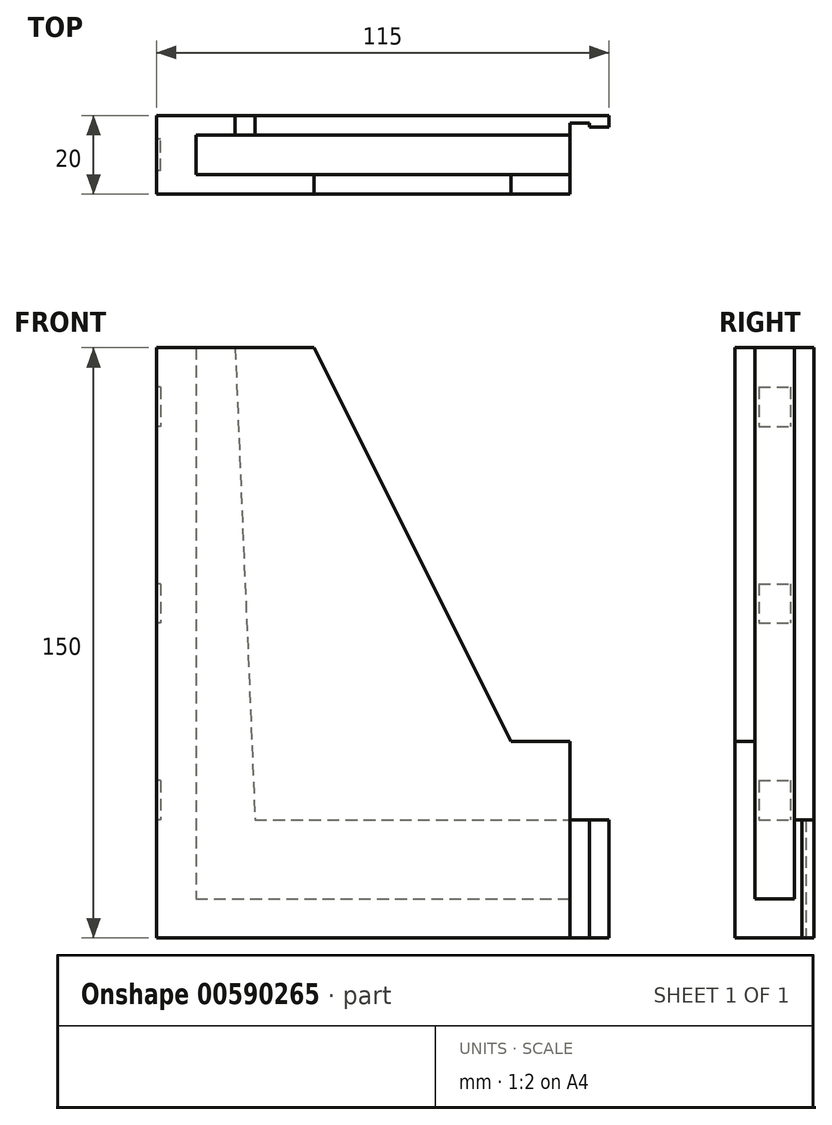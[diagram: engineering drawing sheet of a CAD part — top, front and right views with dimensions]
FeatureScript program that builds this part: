
annotation { "Feature Type Name" : "Feature", "Feature Type Description" : "" }
export const myFeature = defineFeature(function(context is Context, id is Id, definition is map)
    precondition{}
    {
        {
            var Q0;
            Q0=qCreatedBy(makeId("Top.planeOp"),FACE);
            var sketch = newSketch(context, id + "F0", { "sketchPlane" : qUnion([Q0])});
            skLineSegment(sketch, "E0.bottom", {"start": v(0, 0) * mm, "end": v(95, 0) * mm});
            skLineSegment(sketch, "E0.top", {"start": v(0, 5) * mm, "end": v(95, 5) * mm});
            skLineSegment(sketch, "E0.left", {"start": v(0, 0) * mm, "end": v(0, 5) * mm});
            skLineSegment(sketch, "E0.right", {"start": v(95, 0) * mm, "end": v(95, 5) * mm});
            skSolve(sketch);
        }
        {
            var Q0;
            Q0=makeQuery(id+"F0.imprint","IMPRINT",FACE,{"disambiguationData":[TD([[makeQuery(id+"F0.imprint","IMPRINT",EDGE,{"derivedFrom":sQuery(id+"F0.wireOp",EDGE,"E0.bottom")}),1.0]])]});
            extrude(context, id + "F1", {"entities" : qUnion([Q0]), "depth" : 50 * mm, "offsetDistance" : 25 * mm});
        }
        {
            var Q0;
            Q0=qCreatedBy(makeId("Top.planeOp"),FACE);
            var sketch = newSketch(context, id + "F2", { "sketchPlane" : qUnion([Q0])});
            skLineSegment(sketch, "E1.bottom", {"start": v(0, 5) * mm, "end": v(95, 5) * mm});
            skLineSegment(sketch, "E1.top", {"start": v(0, 15) * mm, "end": v(95, 15) * mm});
            skLineSegment(sketch, "E1.left", {"start": v(0, 5) * mm, "end": v(0, 15) * mm});
            skLineSegment(sketch, "E1.right", {"start": v(95, 5) * mm, "end": v(95, 15) * mm});
            skSolve(sketch);
        }
        {
            var Q0;
            Q0 = qSketchRegion(id + "F2", true);
            extrude(context, id + "F3", {"entities" : qUnion([Q0]), "operationType" : NewBodyOperationType.ADD, "depth" : 10 * mm, "offsetDistance" : 25 * mm});
        }
        {
            var Q0;
            Q0=qCreatedBy(makeId("Top.planeOp"),FACE);
            var sketch = newSketch(context, id + "F4", { "sketchPlane" : qUnion([Q0])});
            skLineSegment(sketch, "E2.bottom", {"start": v(0, 15) * mm, "end": v(95, 15) * mm});
            skLineSegment(sketch, "E2.top", {"start": v(0, 20) * mm, "end": v(95, 20) * mm});
            skLineSegment(sketch, "E2.left", {"start": v(0, 15) * mm, "end": v(0, 20) * mm});
            skLineSegment(sketch, "E2.right", {"start": v(95, 15) * mm, "end": v(95, 20) * mm});
            skLineSegment(sketch, "E3.bottom", {"start": v(95, 20) * mm, "end": v(100, 20) * mm});
            skLineSegment(sketch, "E3.top", {"start": v(95, 18) * mm, "end": v(100, 18) * mm});
            skLineSegment(sketch, "E3.left", {"start": v(95, 20) * mm, "end": v(95, 18) * mm});
            skLineSegment(sketch, "E3.right", {"start": v(100, 20) * mm, "end": v(100, 18) * mm});
            skLineSegment(sketch, "E4.bottom", {"start": v(100, 20) * mm, "end": v(105, 20) * mm});
            skLineSegment(sketch, "E4.top", {"start": v(100, 17) * mm, "end": v(105, 17) * mm});
            skLineSegment(sketch, "E4.left", {"start": v(100, 20) * mm, "end": v(100, 17) * mm});
            skLineSegment(sketch, "E4.right", {"start": v(105, 20) * mm, "end": v(105, 17) * mm});
            skSolve(sketch);
        }
        {
            var Q0;
            Q0 = qSketchRegion(id + "F4", true);
            extrude(context, id + "F5", {"entities" : qUnion([Q0]), "operationType" : NewBodyOperationType.ADD, "depth" : 30 * mm, "offsetDistance" : 25 * mm});
        }
        {
            var Q0;
            Q0=makeQuery(id+"F5.opExtrude","SWEPT_FACE",FACE,{"disambiguationData":[OSD([sQuery(id+"F4.wireOp",EDGE,"E2.top"),sQuery(id+"F4.wireOp",EDGE,"E3.bottom"),sQuery(id+"F4.wireOp",EDGE,"E4.bottom")])]});
            var sketch = newSketch(context, id + "F6", { "sketchPlane" : qUnion([Q0])});
            skLineSegment(sketch, "E5.bottom", {"start": v(0, 30) * mm, "end": v(-10, 30) * mm});
            skLineSegment(sketch, "E5.top", {"start": v(0, 150) * mm, "end": v(-10, 150) * mm});
            skLineSegment(sketch, "E5.left", {"start": v(0, 30) * mm, "end": v(0, 150) * mm});
            skLineSegment(sketch, "E5.right", {"start": v(-10, 30) * mm, "end": v(-10, 150) * mm});
            skLineSegment(sketch, "E6", {"start": v(-10, 150) * mm, "end": v(-15, 30) * mm});
            skLineSegment(sketch, "E7", {"start": v(-15, 30) * mm, "end": v(-10, 30) * mm});
            skSolve(sketch);
        }
        {
            var Q0;
            Q0 = qSketchRegion(id + "F6", true);
            extrude(context, id + "F7", {"entities" : qUnion([Q0]), "operationType" : NewBodyOperationType.ADD, "oppositeDirection" : true, "depth" : 5 * mm, "offsetDistance" : 25 * mm});
        }
        {
            var Q0;
            Q0=makeQuery(id+"F1.opExtrude","SWEPT_FACE",FACE,{"disambiguationData":[OSD([sQuery(id+"F0.wireOp",EDGE,"E0.bottom")])]});
            var sketch = newSketch(context, id + "F8", { "sketchPlane" : qUnion([Q0])});
            skLineSegment(sketch, "E8.bottom", {"start": v(0, 50) * mm, "end": v(30, 50) * mm});
            skLineSegment(sketch, "E8.top", {"start": v(0, 150) * mm, "end": v(30, 150) * mm});
            skLineSegment(sketch, "E8.left", {"start": v(0, 50) * mm, "end": v(0, 150) * mm});
            skLineSegment(sketch, "E8.right", {"start": v(30, 50) * mm, "end": v(30, 150) * mm});
            skLineSegment(sketch, "E9", {"start": v(80, 50) * mm, "end": v(30, 150) * mm});
            skLineSegment(sketch, "E10", {"start": v(30, 150) * mm, "end": v(30, 50) * mm});
            skLineSegment(sketch, "E11", {"start": v(30, 50) * mm, "end": v(80, 50) * mm});
            skSolve(sketch);
        }
        {
            var Q0;
            Q0 = qSketchRegion(id + "F8", true);
            extrude(context, id + "F9", {"entities" : qUnion([Q0]), "operationType" : NewBodyOperationType.ADD, "oppositeDirection" : true, "depth" : 5 * mm, "offsetDistance" : 25 * mm});
        }
        {
            var Q0;
            Q0=qCreatedBy(makeId("Top.planeOp"),FACE);
            var sketch = newSketch(context, id + "F10", { "sketchPlane" : qUnion([Q0])});
            skLineSegment(sketch, "E12.bottom", {"start": v(0, 0) * mm, "end": v(-10, 0) * mm});
            skLineSegment(sketch, "E12.top", {"start": v(0, 20) * mm, "end": v(-10, 20) * mm});
            skLineSegment(sketch, "E12.left", {"start": v(0, 0) * mm, "end": v(0, 20) * mm});
            skLineSegment(sketch, "E12.right", {"start": v(-10, 0) * mm, "end": v(-10, 20) * mm});
            skSolve(sketch);
        }
        {
            var Q0;
            Q0 = qSketchRegion(id + "F10", true);
            extrude(context, id + "F11", {"entities" : qUnion([Q0]), "operationType" : NewBodyOperationType.ADD, "depth" : 150 * mm, "offsetDistance" : 25 * mm});
        }
        {
            var Q0;
            Q0=makeQuery(id+"F11.opExtrude","SWEPT_FACE",FACE,{"disambiguationData":[OSD([sQuery(id+"F10.wireOp",EDGE,"E12.right")])]});
            var sketch = newSketch(context, id + "F12", { "sketchPlane" : qUnion([Q0])});
            skLineSegment(sketch, "E13.bottom", {"start": v(-6, 140) * mm, "end": v(-14, 140) * mm});
            skLineSegment(sketch, "E13.top", {"start": v(-6, 130) * mm, "end": v(-14, 130) * mm});
            skLineSegment(sketch, "E13.left", {"start": v(-6, 140) * mm, "end": v(-6, 130) * mm});
            skLineSegment(sketch, "E13.right", {"start": v(-14, 140) * mm, "end": v(-14, 130) * mm});
            skLineSegment(sketch, "E14.bottom", {"start": v(-6, 90) * mm, "end": v(-14, 90) * mm});
            skLineSegment(sketch, "E14.top", {"start": v(-6, 80) * mm, "end": v(-14, 80) * mm});
            skLineSegment(sketch, "E14.left", {"start": v(-6, 90) * mm, "end": v(-6, 80) * mm});
            skLineSegment(sketch, "E14.right", {"start": v(-14, 90) * mm, "end": v(-14, 80) * mm});
            skLineSegment(sketch, "E15.bottom", {"start": v(-6, 40) * mm, "end": v(-14, 40) * mm});
            skLineSegment(sketch, "E15.top", {"start": v(-6, 30) * mm, "end": v(-14, 30) * mm});
            skLineSegment(sketch, "E15.left", {"start": v(-6, 40) * mm, "end": v(-6, 30) * mm});
            skLineSegment(sketch, "E15.right", {"start": v(-14, 40) * mm, "end": v(-14, 30) * mm});
            skSolve(sketch);
        }
        {
            var Q0;
            Q0 = qSketchRegion(id + "F12", true);
            extrude(context, id + "F13", {"entities" : qUnion([Q0]), "operationType" : NewBodyOperationType.REMOVE, "oppositeDirection" : true, "depth" : 1 * mm, "offsetDistance" : 25 * mm});
        }
    });
